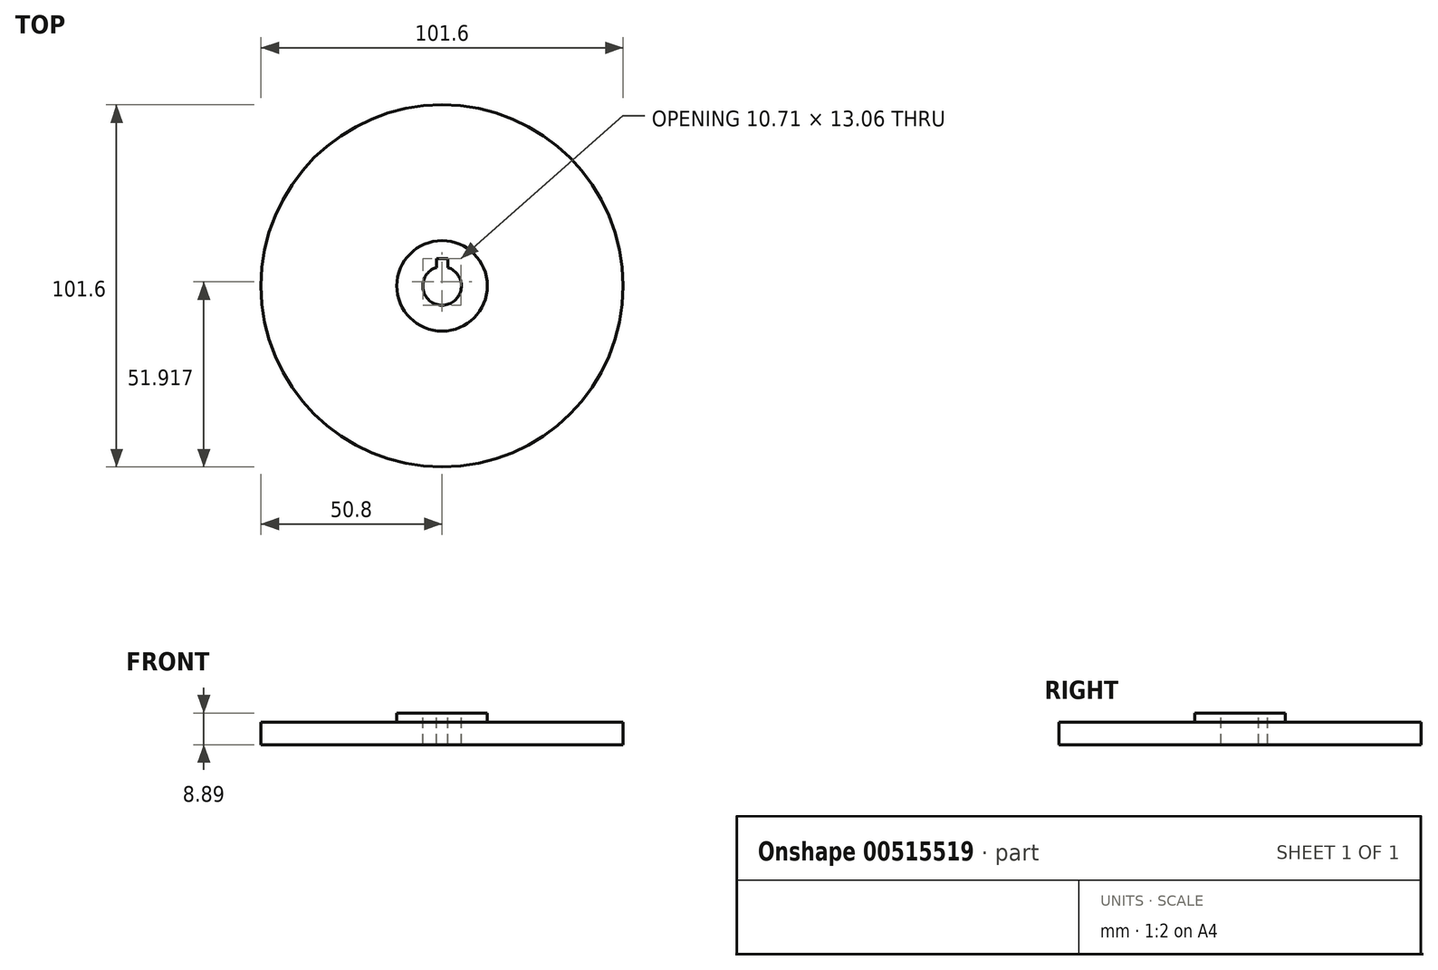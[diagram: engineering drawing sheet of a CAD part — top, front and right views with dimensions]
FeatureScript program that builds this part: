
annotation { "Feature Type Name" : "Feature", "Feature Type Description" : "" }
export const myFeature = defineFeature(function(context is Context, id is Id, definition is map)
    precondition{}
    {
        {
            var Q0;
            Q0=qCreatedBy(makeId("Front.planeOp"),FACE);
            var sketch = newSketch(context, id + "F0", { "sketchPlane" : qUnion([Q0])});
            skLineSegment(sketch, "E0", {"start": v(0, 8.9) * mm, "end": v(-12.7, 8.9) * mm});
            skLineSegment(sketch, "E1", {"start": v(-12.7, 8.9) * mm, "end": v(-12.7, 6.35) * mm});
            skLineSegment(sketch, "E2", {"start": v(-12.7, 6.35) * mm, "end": v(-50.8, 6.35) * mm});
            skLineSegment(sketch, "E3", {"start": v(-50.8, 6.35) * mm, "end": v(-50.8, 0) * mm});
            skLineSegment(sketch, "E4", {"start": v(-50.8, 0) * mm, "end": v(0, 0) * mm});
            skLineSegment(sketch, "E5", {"start": v(0, 0) * mm, "end": v(0, 8.9) * mm});
            skSolve(sketch);
        }
        {
            var Q0;
            Q0=makeQuery(id+"F0.imprint","IMPRINT",FACE,{"disambiguationData":[TD([[makeQuery(id+"F0.imprint","IMPRINT",EDGE,{"derivedFrom":sQuery(id+"F0.wireOp",EDGE,"E0")}),1.0]])]});
            var Q1;
            Q1=sQuery(id+"F0.wireOp",EDGE,"E5");
            revolve(context, id + "F1", {"entities" : qUnion([Q0]), "axis" : qUnion([Q1]), "revolveType" : RevolveType.FULL});
        }
        {
            var Q0;
            Q0=makeQuery(id+"F1.opRevolve","SWEPT_FACE",FACE,{"disambiguationData":[OSD([sQuery(id+"F0.wireOp",EDGE,"E0")])]});
            var sketch = newSketch(context, id + "F2", { "sketchPlane" : qUnion([Q0])});
            skArc(sketch, "E6", {"start": v(-1.59, 5.18) * mm, "mid": v(0, -5.41) * mm, "end": v(1.59, 5.18) * mm});
            skLineSegment(sketch, "E7.bottom", {"start": v(-1.59, 7.65) * mm, "end": v(1.59, 7.65) * mm});
            skLineSegment(sketch, "E7.left", {"start": v(-1.59, 7.65) * mm, "end": v(-1.59, 5.18) * mm});
            skLineSegment(sketch, "E7.right", {"start": v(1.59, 7.65) * mm, "end": v(1.59, 5.18) * mm});
            skSolve(sketch);
        }
        {
            var Q0;
            Q0=makeQuery(id+"F2.imprint","IMPRINT",FACE,{"disambiguationData":[TD([[makeQuery(id+"F2.imprint","IMPRINT",EDGE,{"derivedFrom":sQuery(id+"F2.wireOp",EDGE,"E6")}),1.0]])]});
            extrude(context, id + "F3", {"entities" : qUnion([Q0]), "operationType" : NewBodyOperationType.REMOVE, "oppositeDirection" : true, "depth" : 25.4 * mm, "offsetDistance" : 25.4 * mm});
        }
    });
